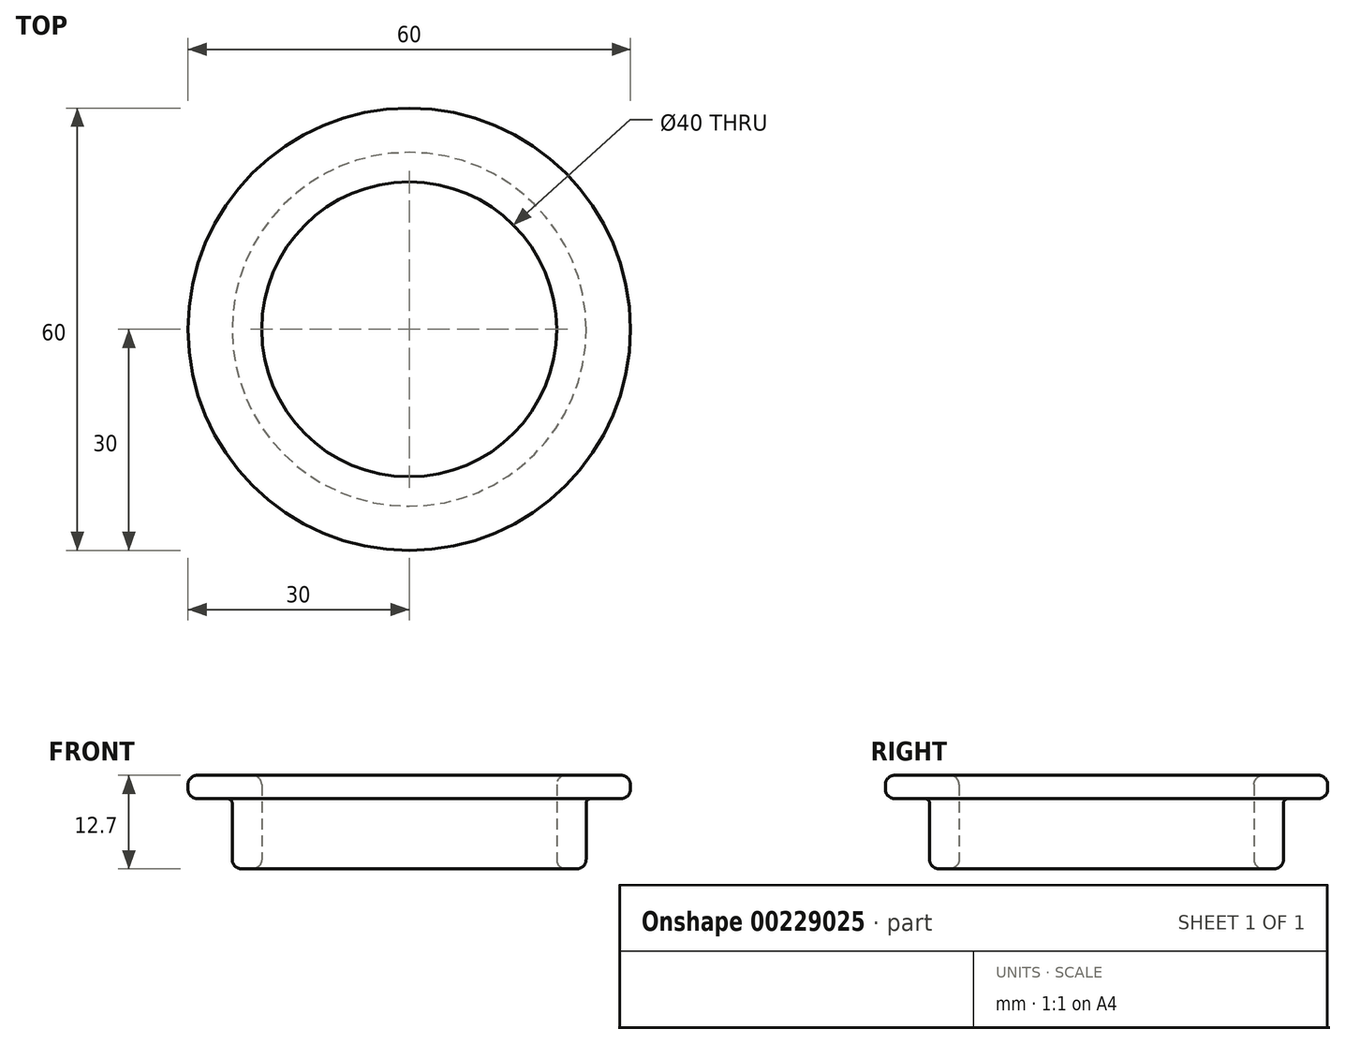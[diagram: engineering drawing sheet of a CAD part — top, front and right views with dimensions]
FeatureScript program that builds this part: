
annotation { "Feature Type Name" : "Feature", "Feature Type Description" : "" }
export const myFeature = defineFeature(function(context is Context, id is Id, definition is map)
    precondition{}
    {
        {
            var Q0;
            Q0=qCreatedBy(makeId("Top.planeOp"),FACE);
            var sketch = newSketch(context, id + "F0", { "sketchPlane" : qUnion([Q0])});
            skCircle(sketch, "E0", {"center": v(0, 0) * mm, "radius": 20 * mm});
            skCircle(sketch, "E1", {"center": v(0, 0) * mm, "radius": 24 * mm});
            skSolve(sketch);
        }
        {
            var Q0;
            Q0=makeQuery(id+"F0.imprint","IMPRINT",FACE,{"disambiguationData":[TD([[makeQuery(id+"F0.imprint","IMPRINT",EDGE,{"derivedFrom":sQuery(id+"F0.wireOp",EDGE,"E0")}),-1.0]])]});
            extrude(context, id + "F1", {"entities" : qUnion([Q0]), "depth" : 12.7 * mm});
        }
        {
            var Q0;
            Q0=makeQuery(id+"F1.opExtrude","CAP_FACE",FACE,{"disambiguationData":[OSD([sQuery(id+"F0.wireOp",EDGE,"E0"),sQuery(id+"F0.wireOp",EDGE,"E1")])],"isStart":false});
            var sketch = newSketch(context, id + "F2", { "sketchPlane" : qUnion([Q0])});
            skCircle(sketch, "E2", {"center": v(0, 0) * mm, "radius": 30 * mm});
            skCircle(sketch, "E3", {"center": v(0, 0) * mm, "radius": 20 * mm});
            skSolve(sketch);
        }
        {
            var Q0;
            Q0 = qSketchRegion(id + "F2", true);
            extrude(context, id + "F3", {"entities" : qUnion([Q0]), "operationType" : NewBodyOperationType.ADD, "oppositeDirection" : true, "depth" : 3.17 * mm});
        }
        {
            var Q0;
            Q0=makeQuery(id+"F1.opExtrude","CAP_EDGE",EDGE,{"disambiguationData":[OSD([sQuery(id+"F0.wireOp",EDGE,"E0")])],"isStart":false});
            var Q1;
            Q1=makeQuery(id+"F1.opExtrude","CAP_EDGE",EDGE,{"disambiguationData":[OSD([sQuery(id+"F0.wireOp",EDGE,"E0")])],"isStart":true});
            var Q2;
            Q2=makeQuery(id+"F3.opExtrude","CAP_EDGE",EDGE,{"disambiguationData":[OSD([sQuery(id+"F2.wireOp",EDGE,"E2")])],"isStart":true});
            var Q3;
            Q3=makeQuery(id+"F3.opExtrude","CAP_EDGE",EDGE,{"disambiguationData":[OSD([sQuery(id+"F2.wireOp",EDGE,"E2")])],"isStart":false});
            var Q4;
            Q4=makeQuery(id+"F1.opExtrude","CAP_EDGE",EDGE,{"disambiguationData":[OSD([sQuery(id+"F0.wireOp",EDGE,"E1")])],"isStart":true});
            fillet(context, id + "F4", {"entities" : qUnion([Q0, Q1, Q2, Q3, Q4]), "radius" : 1.27 * mm, "tangentPropagation" : true, "allowEdgeOverflow" : false});
        }
        {
            var Q0;
            Q0=makeQuery(id+"F3.boolean.opBoolean","INTERSECT",EDGE,{"derivedFrom":[makeQuery(id+"F1.opExtrude","SWEPT_FACE",FACE,{"disambiguationData":[OSD([sQuery(id+"F0.wireOp",EDGE,"E1")])]}),makeQuery(id+"F3.opExtrude","CAP_FACE",FACE,{"disambiguationData":[OSD([sQuery(id+"F2.wireOp",EDGE,"E2"),sQuery(id+"F2.wireOp",EDGE,"E3")])],"isStart":false})]});
            fillet(context, id + "F5", {"entities" : qUnion([Q0]), "radius" : 0.64 * mm, "tangentPropagation" : true, "allowEdgeOverflow" : false});
        }
    });
